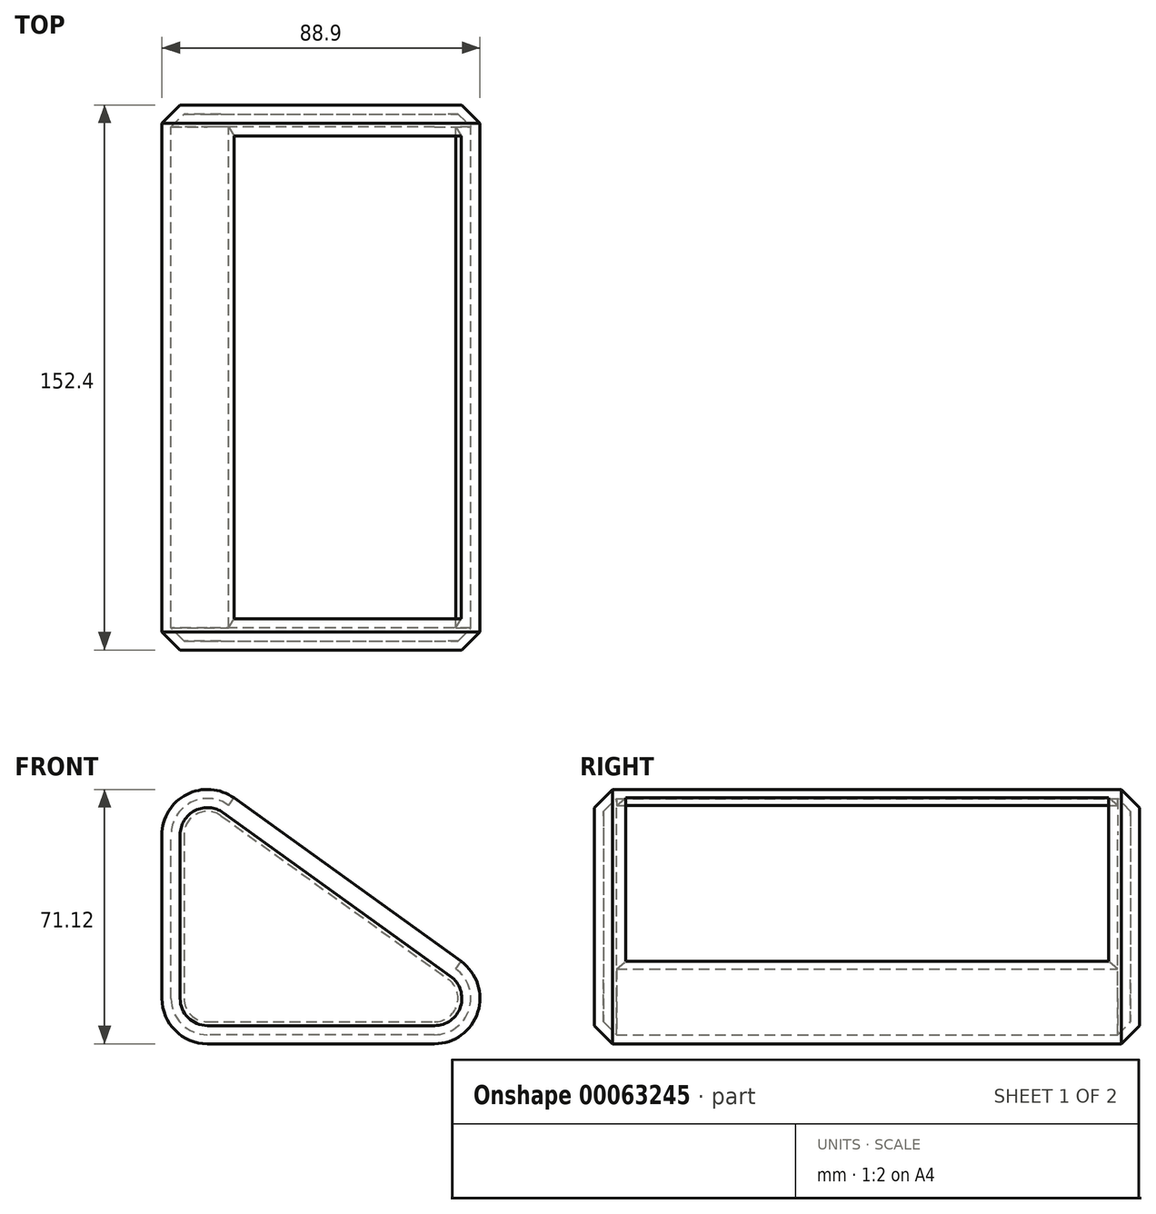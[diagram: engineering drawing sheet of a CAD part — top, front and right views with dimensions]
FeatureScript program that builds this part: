
annotation { "Feature Type Name" : "Feature", "Feature Type Description" : "" }
export const myFeature = defineFeature(function(context is Context, id is Id, definition is map)
    precondition{}
    {
        {
            var Q0;
            Q0=qCreatedBy(makeId("Front.planeOp"),FACE);
            var sketch = newSketch(context, id + "F0", { "sketchPlane" : qUnion([Q0])});
            skLineSegment(sketch, "E0", {"start": v(0, 45.72) * mm, "end": v(0, 0) * mm, "construction": true});
            skLineSegment(sketch, "E1", {"start": v(0, 0) * mm, "end": v(63.5, 0) * mm, "construction": true});
            skCircle(sketch, "E2", {"center": v(0, 45.72) * mm, "radius": 12.7 * mm});
            skCircle(sketch, "E3", {"center": v(0, 0) * mm, "radius": 12.7 * mm});
            skCircle(sketch, "E4", {"center": v(63.5, 0) * mm, "radius": 12.7 * mm});
            skLineSegment(sketch, "E5", {"start": v(7.42, 56.03) * mm, "end": v(70.92, 10.3) * mm});
            skLineSegment(sketch, "E6", {"start": v(-12.7, 45.72) * mm, "end": v(-12.7, 0) * mm});
            skLineSegment(sketch, "E7", {"start": v(0, -12.7) * mm, "end": v(63.5, -12.7) * mm});
            skSolve(sketch);
        }
        {
            var Q0;
            Q0 = qSketchRegion(id + "F0", true);
            extrude(context, id + "F1", {"entities" : qUnion([Q0]), "depth" : 127 * mm, "hasSecondDirection" : true, "secondDirectionOppositeDirection" : true, "secondDirectionDepth" : 25.4 * mm});
        }
        {
            var Q0;
            Q0=makeQuery(id+"F1.opExtrude","SWEPT_FACE",FACE,{"disambiguationData":[OSD([sQuery(id+"F0.wireOp",EDGE,"E5")])]});
            chamfer(context, id + "F2", {"entities" : qUnion([Q0]), "width" : 5.08 * mm, "tangentPropagation" : true});
        }
        {
            var Q0;
            Q0=makeQuery(id+"F1.opExtrude","SWEPT_FACE",FACE,{"disambiguationData":[OSD([sQuery(id+"F0.wireOp",EDGE,"E5")])]});
            shell(context, id + "F3", {"entities" : qUnion([Q0]), "thickness" : 2.54 * mm});
        }
    });
